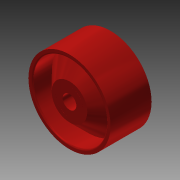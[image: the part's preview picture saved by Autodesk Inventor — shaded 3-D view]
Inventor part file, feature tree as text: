
AUTODESK INVENTOR PART (.ipt)
format: ipt  version: 2014 (Build 180170000, 170)  size: 144,896 bytes
history: native  units: mm
features: extrude x4, sketch x2, chamfer x2, fillet x2
ambient origin geometry x8: Origin, YZ Plane, XZ Plane, XY Plane, X Axis, Y Axis, Z Axis, Center Point
bodies: Solid1 (feature_tree), Solid2 (feature_tree), Solid3 (feature_tree)
feature tree (10):
  sketch  "Sketch1"  dims[d0=30.0mm d1=27.0mm]
  extrude  "Extrusion1"  Depth=27.0mm
  extrude  "Extrusion3"  Depth=15.0mm TaperAngle=0.0deg
  chamfer  "Chamfer1"  Distance=15.0mm
  chamfer  "Chamfer2"  Distance=7.0mm Angle=45.0deg
  fillet  "Fillet1"  Radius=5.0mm
  fillet  "Fillet2"  Radius=0.5mm
  extrude  "Extrusion4"  Depth=0.5mm
  extrude  "Extrusion5"  Depth=15.0mm TaperAngle=0.0deg
  sketch  "Sketch2"  dims[d2=10.0mm d3=15.0mm d4=0.0mm d7=15.0mm d8=0.0mm d9=7.0mm d10=2.0mm d11=45.0deg d12=7.0mm d13=5.0mm d14=45.0deg d15=0.5mm d16=0.5mm d17=15.0mm d18=0.0mm d19=5.0mm d20=15.0mm d21=0.0mm]
